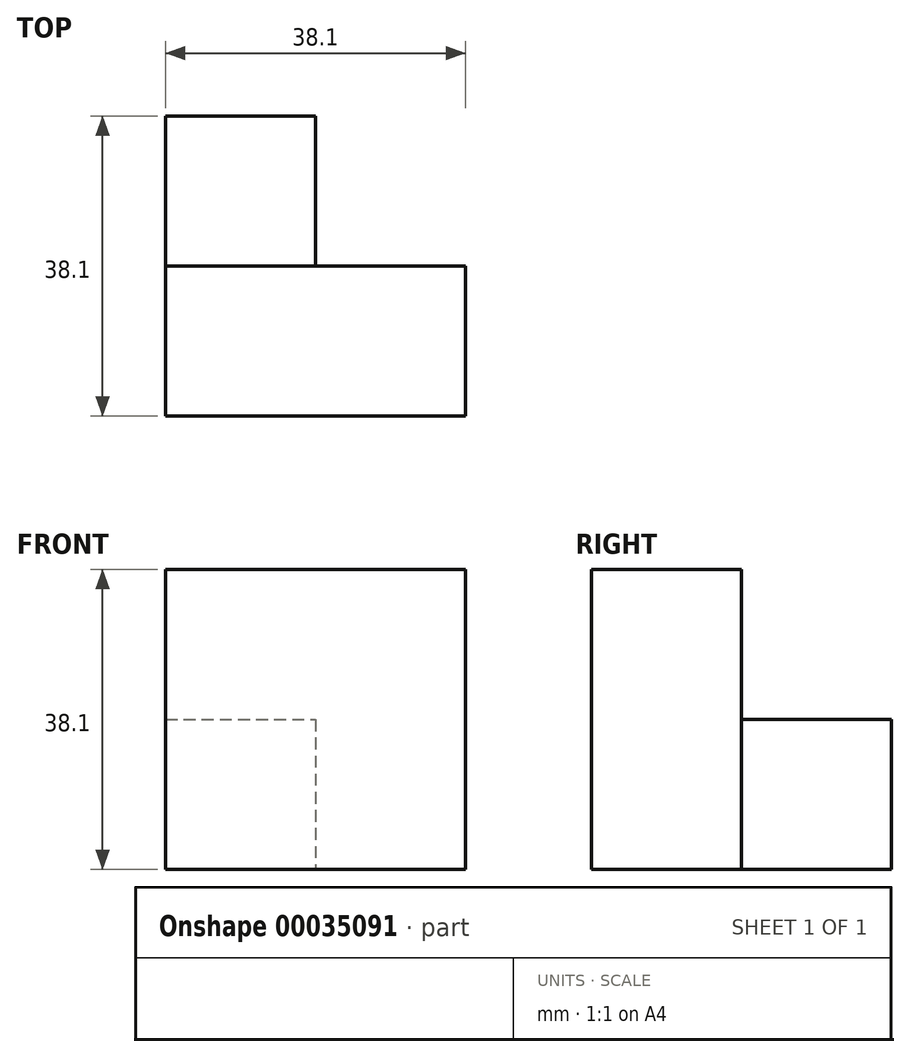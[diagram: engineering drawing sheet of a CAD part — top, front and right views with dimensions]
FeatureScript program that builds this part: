
annotation { "Feature Type Name" : "Feature", "Feature Type Description" : "" }
export const myFeature = defineFeature(function(context is Context, id is Id, definition is map)
    precondition{}
    {
        {
            var Q0;
            Q0=qCreatedBy(makeId("Front.planeOp"),FACE);
            var sketch = newSketch(context, id + "F0", { "sketchPlane" : qUnion([Q0])});
            skLineSegment(sketch, "E0", {"start": v(22.42, 9.46) * mm, "end": v(60.52, 9.46) * mm});
            skLineSegment(sketch, "E1", {"start": v(60.52, 9.46) * mm, "end": v(60.52, -28.64) * mm});
            skLineSegment(sketch, "E2", {"start": v(60.52, -28.64) * mm, "end": v(22.42, -28.64) * mm});
            skLineSegment(sketch, "E3", {"start": v(22.42, -28.64) * mm, "end": v(22.42, 9.46) * mm});
            skSolve(sketch);
        }
        {
            var Q0;
            Q0 = qSketchRegion(id + "F0", true);
            extrude(context, id + "F1", {"entities" : qUnion([Q0]), "depth" : 19.05 * mm});
        }
        {
            var Q0;
            Q0=makeQuery(id+"F1.opExtrude","CAP_FACE",FACE,{"disambiguationData":[OSD([sQuery(id+"F0.wireOp",EDGE,"E0"),sQuery(id+"F0.wireOp",EDGE,"E1"),sQuery(id+"F0.wireOp",EDGE,"E2"),sQuery(id+"F0.wireOp",EDGE,"E3")])],"isStart":true});
            var sketch = newSketch(context, id + "F2", { "sketchPlane" : qUnion([Q0])});
            skLineSegment(sketch, "E4", {"start": v(-22.42, -9.6) * mm, "end": v(-41.47, -9.6) * mm});
            skLineSegment(sketch, "E5", {"start": v(-41.47, -9.6) * mm, "end": v(-41.47, -28.64) * mm});
            skLineSegment(sketch, "E6", {"start": v(-41.47, -28.64) * mm, "end": v(-22.42, -28.64) * mm});
            skLineSegment(sketch, "E7", {"start": v(-22.42, -28.64) * mm, "end": v(-22.42, -9.6) * mm});
            skSolve(sketch);
        }
        {
            var Q0;
            Q0 = qSketchRegion(id + "F2", true);
            extrude(context, id + "F3", {"entities" : qUnion([Q0]), "operationType" : NewBodyOperationType.ADD, "depth" : 19.05 * mm});
        }
    });
